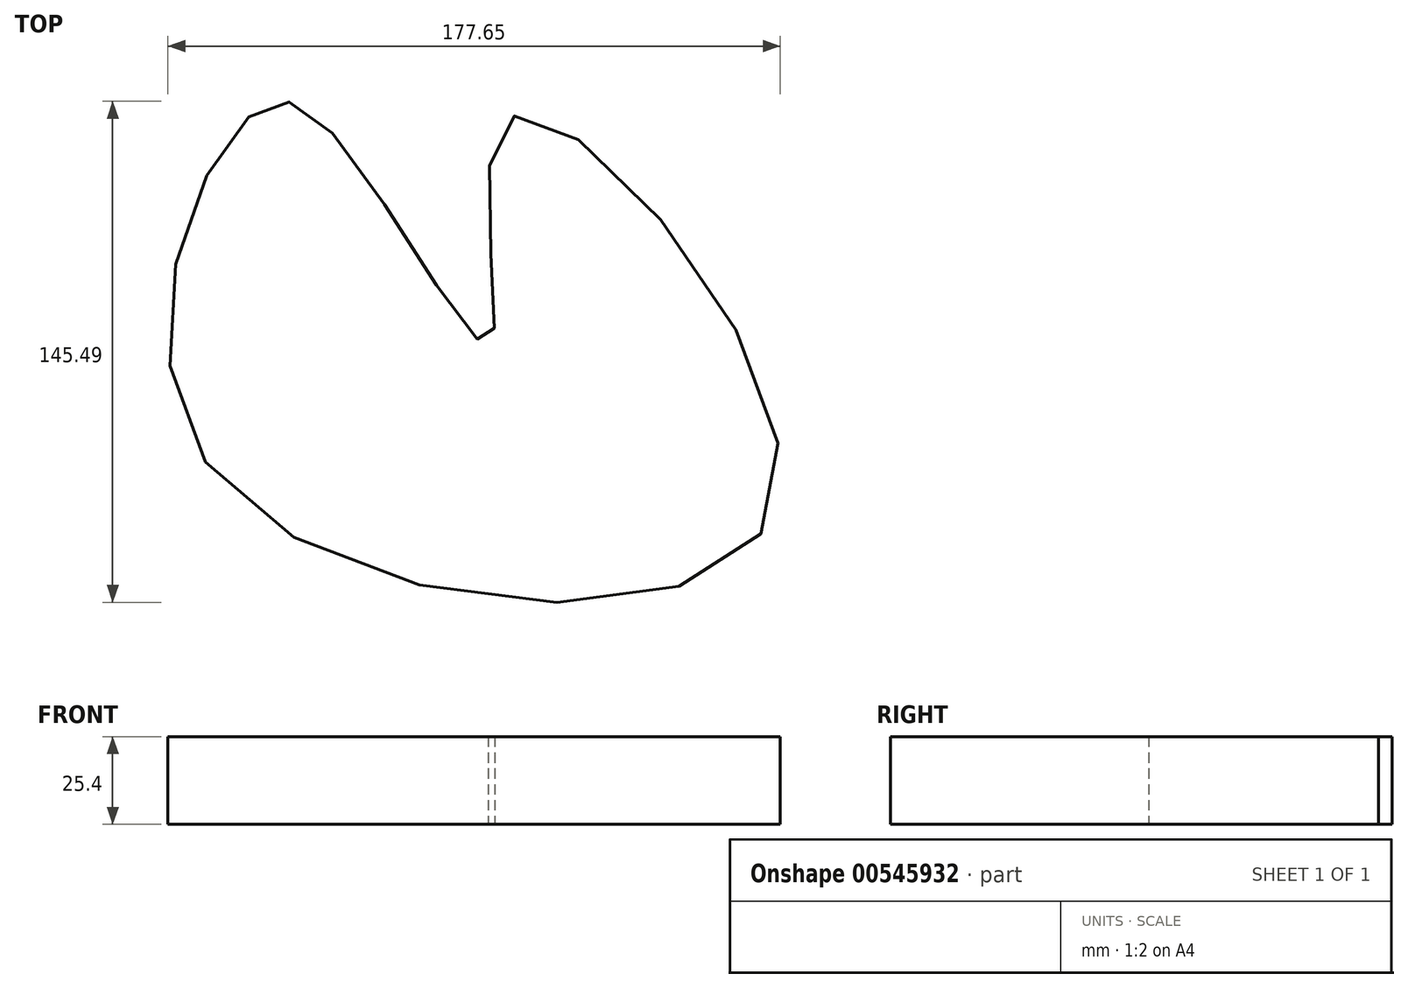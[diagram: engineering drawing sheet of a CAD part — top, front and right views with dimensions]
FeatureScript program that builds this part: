
annotation { "Feature Type Name" : "Feature", "Feature Type Description" : "" }
export const myFeature = defineFeature(function(context is Context, id is Id, definition is map)
    precondition{}
    {
        {
            var Q0;
            Q0=qCreatedBy(makeId("Top.planeOp"),FACE);
            var sketch = newSketch(context, id + "F0", { "sketchPlane" : qUnion([Q0])});
            skFitSpline(sketch, "E0", {"points": [v(-89.3, 77.54) * mm, v(-98.57, -26.88) * mm, v(63.48, -35.4) * mm, v(-13.57, 77.23) * mm, v(-18.97, 12.06) * mm, v(-63.7, 71.31) * mm, v(-89.3, 77.54) * mm]});
            skSolve(sketch);
        }
        {
            var Q0;
            Q0 = qSketchRegion(id + "F0", true);
            extrude(context, id + "F1", {"entities" : qUnion([Q0]), "depth" : 25.4 * mm, "offsetDistance" : 25.4 * mm});
        }
        {
            var Q0;
            Q0=qCreatedBy(makeId("Top.planeOp"),FACE);
            var sketch = newSketch(context, id + "F2", { "sketchPlane" : qUnion([Q0])});
            skCircle(sketch, "E1", {"center": v(-108.73, 71.33) * mm, "radius": 17.6 * mm});
            skSolve(sketch);
        }
        {
            var Q0;
            Q0=sQuery(id+"F2.wireOp",EDGE,"E1");
            extrude(context, id + "F3", {"bodyType" : ToolBodyType.SURFACE, "surfaceEntities" : qUnion([Q0]), "depth" : 25.4 * mm, "offsetDistance" : 25.4 * mm});
        }
    });
